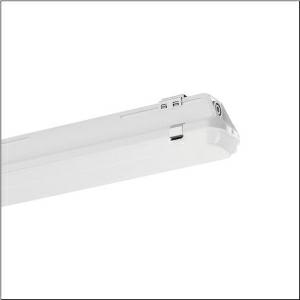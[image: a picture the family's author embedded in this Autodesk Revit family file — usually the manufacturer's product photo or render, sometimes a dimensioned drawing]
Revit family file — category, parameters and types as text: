
# Revit family: monsun_r__21_51fb207p430k_d90a
name_source: partatom
category: Lighting Fixtures
units: mm (PartAtom-declared; Revit-internal decimal feet)

## family parameters
Cut with Voids When Loaded = No
Host = Face
Light Source = No
Part Type = Normal
Room Calculation Point = No
Round Connector Dimension = Use Diameter
Shared = No

## types (1)
- Monsun® 21 (1 x LED, 3550 lm, 22.1 W, 4000K)
    Apparent Load = 22 VA
    CIE Flux Codes = 45 75 93 94 100
    Color Rendering = 80
    Color Temperature = 4000K
    Default Elevation = 1800 mm
    Description = Monsun® 21, damp-proof luminaire, chain hanger, primary optical cover: enclosure, of PC, light emission: direct distribution, primary light characteristic: symmetric, installation type: suspended mounting, surface-mounted, horizontal mounting, vertical mounting, LED, rated luminous flux: 3.550lm, luminous efficacy: 161lm/W, light colour: 840, colour temperature: 4000K, control gear: ON/OFF, with terminal, 3-pole, max. 2.5mm², mains connection: 220..240V, AC, 50/60Hz, rated input power: 22W, housing, of glass-fibre reinforced polyester, uncoated, bright grey, incl. chain hanger, length: 1.590mm, width: 90mm, height: 88mm, clip for enclosure, of stainless steel (V2A), ceiling mounting element, of stainless steel (V2A), chain hanger, of stainless steel (V2A), protection rating (complete): IP66, insulation class (complete): insulation class I (protective earthing), certification: CE, ENEC, VDE, UKCA, protection symbol: D, impact resistance: IK08, permissible operating ambient temperature: -25..+35°C, standard: EN 50419, EN 60598-2-1, corresponds to IFS (International Featured Standards) requirements for safety and quality in the food industry, for indoor or canopied outdoor use, no direct snow, no direct sun, no direct rain, LABS conformity tested according to VDMA 24364:2018-05, contact your sales advisor before using the luminaires in applications with unclear chemical exposure, large temperature fluctuations or condensation-forming humidity, packaging unit: 1 piece
    Height = 89 mm
    Lamp = 1 x LED
    Lamp Light Flux = 3550 lm
    Lamp Power = 22.1 W
    Lamp count = 1
    Length = 1590 mm
    Luminous efficacy = 161 lm/W
    Manufacturer = Siteco
    ModVariant = No
    Model = 51FB207P430K
    Mounting Place = Ceiling
    Mounting Type = Surface mounted
    Number of Poles = 1
    OnlyDefault = Yes
    Power Factor = 1
    Product Name = Monsun® 21
    Product group = damp-proof luminaire
    ProductGroupID = 300
    Protection Class = Protection class I
    Protection Degree = IP 66
    RLX_Detail_Level = 1
    RLX_Emergency_Light_Flux = 0 lm
    RLX_Emergency_Type = 0
    RLX_Emergency_Type_DB = No
    RlxData = <blob elided: 88665 chars, md5=2569af75>
    Socket = socket
    Standby Power = 0 W
    System Light Flux = 3550 lm
    System Power = 22 W
    Type Comments = Product without accessories
    Type Image = l_1319656.jpg
    URL = http://relux.com
    VarID = ---
    Voltage = 0 V
    Weight = 0.00 kg
    Width = 90 mm

## geometry (parser evidence)
native form markers: Blend x4, Sweep x12
no freeform markers — native parametric forms only
